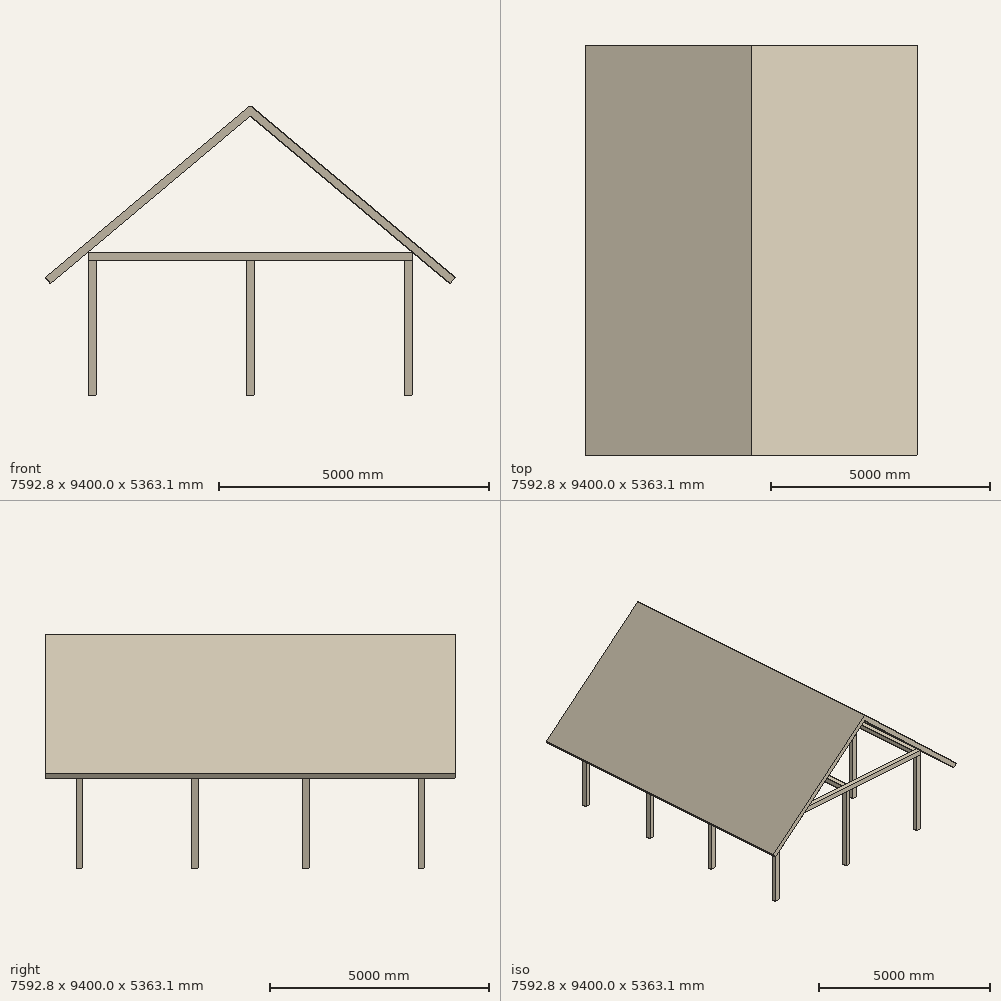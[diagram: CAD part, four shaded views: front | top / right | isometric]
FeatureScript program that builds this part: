
annotation { "Feature Type Name" : "Feature", "Feature Type Description" : "" }
export const myFeature = defineFeature(function(context is Context, id is Id, definition is map)
    precondition{}
    {
        {
            var Q0;
            Q0=qCreatedBy(makeId("Top.planeOp"),FACE);
            var sketch = newSketch(context, id + "F0", { "sketchPlane" : qUnion([Q0])});
            skLineSegment(sketch, "E0.bottom", {"start": v(-3000, 4000) * mm, "end": v(3000, 4000) * mm});
            skLineSegment(sketch, "E0.top", {"start": v(-3000, -4000) * mm, "end": v(3000, -4000) * mm});
            skLineSegment(sketch, "E0.left", {"start": v(-3000, 4000) * mm, "end": v(-3000, -4000) * mm});
            skLineSegment(sketch, "E0.right", {"start": v(3000, 4000) * mm, "end": v(3000, -4000) * mm});
            skSolve(sketch);
        }
        {
            var Q0;
            Q0=makeQuery(id+"F0.imprint","IMPRINT",FACE,{"disambiguationData":[TD([[makeQuery(id+"F0.imprint","IMPRINT",EDGE,{"derivedFrom":sQuery(id+"F0.wireOp",EDGE,"E0.bottom")}),-1.0]])]});
            extrude(context, id + "F1", {"entities" : qUnion([Q0]), "depth" : 2500 * mm});
        }
        {
            var Q0;
            Q0=makeQuery(id+"F1.opExtrude","SWEPT_FACE",FACE,{"disambiguationData":[OSD([sQuery(id+"F0.wireOp",EDGE,"E0.left")])]});
            var sketch = newSketch(context, id + "F2", { "sketchPlane" : qUnion([Q0])});
            skLineSegment(sketch, "E1.bottom", {"start": v(-3850, 0) * mm, "end": v(-1350, 0) * mm});
            skLineSegment(sketch, "E1.top", {"start": v(-3850, 2500) * mm, "end": v(-1350, 2500) * mm});
            skLineSegment(sketch, "E1.left", {"start": v(-3850, 0) * mm, "end": v(-3850, 2500) * mm});
            skLineSegment(sketch, "E1.right", {"start": v(-1350, 0) * mm, "end": v(-1350, 2500) * mm});
            skLineSegment(sketch, "E2.bottom", {"start": v(3850, 2500) * mm, "end": v(1350, 2500) * mm});
            skLineSegment(sketch, "E2.top", {"start": v(3850, 0) * mm, "end": v(1350, 0) * mm});
            skLineSegment(sketch, "E2.left", {"start": v(3850, 2500) * mm, "end": v(3850, 0) * mm});
            skLineSegment(sketch, "E2.right", {"start": v(1350, 2500) * mm, "end": v(1350, 0) * mm});
            skLineSegment(sketch, "E3.bottom", {"start": v(-1200, 2500) * mm, "end": v(1200, 2500) * mm});
            skLineSegment(sketch, "E3.top", {"start": v(-1200, 0) * mm, "end": v(1200, 0) * mm});
            skLineSegment(sketch, "E3.left", {"start": v(-1200, 2500) * mm, "end": v(-1200, 0) * mm});
            skLineSegment(sketch, "E3.right", {"start": v(1200, 2500) * mm, "end": v(1200, 0) * mm});
            skSolve(sketch);
        }
        {
            var Q0;
            Q0=makeQuery(id+"F2.imprint","IMPRINT",FACE,{"disambiguationData":[TD([[makeQuery(id+"F2.imprint","IMPRINT",EDGE,{"derivedFrom":sQuery(id+"F2.wireOp",EDGE,"E1.bottom")}),1.0]])]});
            var Q1;
            Q1=makeQuery(id+"F2.imprint","IMPRINT",FACE,{"disambiguationData":[TD([[makeQuery(id+"F2.imprint","IMPRINT",EDGE,{"derivedFrom":sQuery(id+"F2.wireOp",EDGE,"E3.bottom")}),-1.0]])]});
            var Q2;
            Q2=makeQuery(id+"F2.imprint","IMPRINT",FACE,{"disambiguationData":[TD([[makeQuery(id+"F2.imprint","IMPRINT",EDGE,{"derivedFrom":sQuery(id+"F2.wireOp",EDGE,"E2.bottom")}),-1.0]])]});
            extrude(context, id + "F3", {"entities" : qUnion([Q0, Q1, Q2]), "operationType" : NewBodyOperationType.REMOVE, "endBound" : BoundingType.THROUGH_ALL, "oppositeDirection" : true, "depth" : 25 * mm});
        }
        {
            var Q0;
            Q0=makeQuery(id+"F1.opExtrude","SWEPT_FACE",FACE,{"disambiguationData":[OSD([sQuery(id+"F0.wireOp",EDGE,"E0.top")])]});
            var sketch = newSketch(context, id + "F4", { "sketchPlane" : qUnion([Q0])});
            skLineSegment(sketch, "E4.bottom", {"start": v(-2850, 2500) * mm, "end": v(-75, 2500) * mm});
            skLineSegment(sketch, "E4.top", {"start": v(-2850, 0) * mm, "end": v(-75, 0) * mm});
            skLineSegment(sketch, "E4.left", {"start": v(-2850, 2500) * mm, "end": v(-2850, 0) * mm});
            skLineSegment(sketch, "E4.right", {"start": v(-75, 2500) * mm, "end": v(-75, 0) * mm});
            skLineSegment(sketch, "E5.bottom", {"start": v(75, 2500) * mm, "end": v(2850, 2500) * mm});
            skLineSegment(sketch, "E5.top", {"start": v(75, 0) * mm, "end": v(2850, 0) * mm});
            skLineSegment(sketch, "E5.left", {"start": v(75, 2500) * mm, "end": v(75, 0) * mm});
            skLineSegment(sketch, "E5.right", {"start": v(2850, 2500) * mm, "end": v(2850, 0) * mm});
            skSolve(sketch);
        }
        {
            var Q0;
            Q0=makeQuery(id+"F4.imprint","IMPRINT",FACE,{"disambiguationData":[TD([[makeQuery(id+"F4.imprint","IMPRINT",EDGE,{"derivedFrom":sQuery(id+"F4.wireOp",EDGE,"E4.bottom")}),-1.0]])]});
            var Q1;
            Q1=makeQuery(id+"F4.imprint","IMPRINT",FACE,{"disambiguationData":[TD([[makeQuery(id+"F4.imprint","IMPRINT",EDGE,{"derivedFrom":sQuery(id+"F4.wireOp",EDGE,"E5.bottom")}),-1.0]])]});
            extrude(context, id + "F5", {"entities" : qUnion([Q0, Q1]), "operationType" : NewBodyOperationType.REMOVE, "endBound" : BoundingType.THROUGH_ALL, "oppositeDirection" : true, "depth" : 25 * mm});
        }
        {
            var Q0;
            {var subQ0=sQuery(id+"F0.wireOp",EDGE,"E0.top");var subQ1=makeQuery(id+"F1.opExtrude","SWEPT_FACE",FACE,{"disambiguationData":[OSD([subQ0])]});var subQ2=sQuery(id+"F0.wireOp",EDGE,"E0.right");var subQ3=makeQuery(id+"F1.opExtrude","SWEPT_FACE",FACE,{"disambiguationData":[OSD([subQ2])]});var subQ5=sQuery(id+"F0.wireOp",EDGE,"E0.left");Q0=makeQuery(id+"F5.boolean.opBoolean","SPLIT",FACE,{"disambiguationData":[TD([subQ3])],"derivedFrom":makeQuery(id+"F3.boolean.opBoolean","SPLIT",FACE,{"disambiguationData":[TD([subQ1])],"derivedFrom":makeQuery(id+"F1.opExtrude","CAP_FACE",FACE,{"disambiguationData":[OSD([sQuery(id+"F0.wireOp",EDGE,"E0.bottom"),subQ0,subQ5,subQ2])],"isStart":false})})});}
            var sketch = newSketch(context, id + "F6", { "sketchPlane" : qUnion([Q0])});
            skLineSegment(sketch, "E6.bottom", {"start": v(3000, -4000) * mm, "end": v(-3000, -4000) * mm});
            skLineSegment(sketch, "E6.top", {"start": v(3000, -3850) * mm, "end": v(-3000, -3850) * mm});
            skLineSegment(sketch, "E6.left", {"start": v(3000, -4000) * mm, "end": v(3000, -3850) * mm});
            skLineSegment(sketch, "E6.right", {"start": v(-3000, -4000) * mm, "end": v(-3000, -3850) * mm});
            skLineSegment(sketch, "E7.bottom", {"start": v(3000, -1350) * mm, "end": v(-3000, -1350) * mm});
            skLineSegment(sketch, "E7.top", {"start": v(3000, -1200) * mm, "end": v(-3000, -1200) * mm});
            skLineSegment(sketch, "E7.left", {"start": v(3000, -1350) * mm, "end": v(3000, -1200) * mm});
            skLineSegment(sketch, "E7.right", {"start": v(-3000, -1350) * mm, "end": v(-3000, -1200) * mm});
            skLineSegment(sketch, "E8.bottom", {"start": v(-3000, 1200) * mm, "end": v(3000, 1200) * mm});
            skLineSegment(sketch, "E8.top", {"start": v(-3000, 1350) * mm, "end": v(3000, 1350) * mm});
            skLineSegment(sketch, "E8.left", {"start": v(-3000, 1200) * mm, "end": v(-3000, 1350) * mm});
            skLineSegment(sketch, "E8.right", {"start": v(3000, 1200) * mm, "end": v(3000, 1350) * mm});
            skLineSegment(sketch, "E9.bottom", {"start": v(3000, 3850) * mm, "end": v(-3000, 3850) * mm});
            skLineSegment(sketch, "E9.top", {"start": v(3000, 4000) * mm, "end": v(-3000, 4000) * mm});
            skLineSegment(sketch, "E9.left", {"start": v(3000, 3850) * mm, "end": v(3000, 4000) * mm});
            skLineSegment(sketch, "E9.right", {"start": v(-3000, 3850) * mm, "end": v(-3000, 4000) * mm});
            skLineSegment(sketch, "E10.bottom", {"start": v(-3000, 3850) * mm, "end": v(-2850, 3850) * mm, "construction": true});
            skLineSegment(sketch, "E10.top", {"start": v(-3000, 1350) * mm, "end": v(-2850, 1350) * mm, "construction": true});
            skLineSegment(sketch, "E10.left", {"start": v(-3000, 3850) * mm, "end": v(-3000, 1350) * mm});
            skLineSegment(sketch, "E10.right", {"start": v(-2850, 3850) * mm, "end": v(-2850, 1350) * mm});
            skLineSegment(sketch, "E11.bottom", {"start": v(-3000, 1200) * mm, "end": v(-2850, 1200) * mm, "construction": true});
            skLineSegment(sketch, "E11.top", {"start": v(-3000, -1200) * mm, "end": v(-2850, -1200) * mm, "construction": true});
            skLineSegment(sketch, "E11.left", {"start": v(-3000, 1200) * mm, "end": v(-3000, -1200) * mm});
            skLineSegment(sketch, "E11.right", {"start": v(-2850, 1200) * mm, "end": v(-2850, -1200) * mm});
            skLineSegment(sketch, "E12.bottom", {"start": v(-3000, -1350) * mm, "end": v(-2850, -1350) * mm, "construction": true});
            skLineSegment(sketch, "E12.top", {"start": v(-3000, -3850) * mm, "end": v(-2850, -3850) * mm, "construction": true});
            skLineSegment(sketch, "E12.left", {"start": v(-3000, -1350) * mm, "end": v(-3000, -3850) * mm});
            skLineSegment(sketch, "E12.right", {"start": v(-2850, -1350) * mm, "end": v(-2850, -3850) * mm});
            skLineSegment(sketch, "E13.bottom", {"start": v(3000, -1350) * mm, "end": v(2850, -1350) * mm, "construction": true});
            skLineSegment(sketch, "E13.top", {"start": v(3000, -3850) * mm, "end": v(2850, -3850) * mm, "construction": true});
            skLineSegment(sketch, "E13.left", {"start": v(3000, -1350) * mm, "end": v(3000, -3850) * mm});
            skLineSegment(sketch, "E13.right", {"start": v(2850, -1350) * mm, "end": v(2850, -3850) * mm});
            skLineSegment(sketch, "E14.bottom", {"start": v(75, -1350) * mm, "end": v(-75, -1350) * mm, "construction": true});
            skLineSegment(sketch, "E14.top", {"start": v(75, -3850) * mm, "end": v(-75, -3850) * mm, "construction": true});
            skLineSegment(sketch, "E14.left", {"start": v(75, -1350) * mm, "end": v(75, -3850) * mm});
            skLineSegment(sketch, "E14.right", {"start": v(-75, -1350) * mm, "end": v(-75, -3850) * mm});
            skLineSegment(sketch, "E15.bottom", {"start": v(75, 1200) * mm, "end": v(-75, 1200) * mm, "construction": true});
            skLineSegment(sketch, "E15.top", {"start": v(75, -1200) * mm, "end": v(-75, -1200) * mm, "construction": true});
            skLineSegment(sketch, "E15.left", {"start": v(75, 1200) * mm, "end": v(75, -1200) * mm});
            skLineSegment(sketch, "E15.right", {"start": v(-75, 1200) * mm, "end": v(-75, -1200) * mm});
            skLineSegment(sketch, "E16.bottom", {"start": v(3000, 1200) * mm, "end": v(2850, 1200) * mm, "construction": true});
            skLineSegment(sketch, "E16.top", {"start": v(3000, -1200) * mm, "end": v(2850, -1200) * mm, "construction": true});
            skLineSegment(sketch, "E16.left", {"start": v(3000, 1200) * mm, "end": v(3000, -1200) * mm});
            skLineSegment(sketch, "E16.right", {"start": v(2850, 1200) * mm, "end": v(2850, -1200) * mm});
            skLineSegment(sketch, "E17.bottom", {"start": v(3000, 3850) * mm, "end": v(2850, 3850) * mm, "construction": true});
            skLineSegment(sketch, "E17.top", {"start": v(3000, 1350) * mm, "end": v(2850, 1350) * mm, "construction": true});
            skLineSegment(sketch, "E17.left", {"start": v(3000, 3850) * mm, "end": v(3000, 1350) * mm});
            skLineSegment(sketch, "E17.right", {"start": v(2850, 3850) * mm, "end": v(2850, 1350) * mm});
            skLineSegment(sketch, "E18.bottom", {"start": v(75, 3850) * mm, "end": v(-75, 3850) * mm, "construction": true});
            skLineSegment(sketch, "E18.top", {"start": v(75, 1350) * mm, "end": v(-75, 1350) * mm, "construction": true});
            skLineSegment(sketch, "E18.left", {"start": v(75, 3850) * mm, "end": v(75, 1350) * mm});
            skLineSegment(sketch, "E18.right", {"start": v(-75, 3850) * mm, "end": v(-75, 1350) * mm});
            skSolve(sketch);
        }
        {
            var Q0;
            {var subQ8=sQuery(id+"F6.wireOp",EDGE,"E6.right");Q0=makeQuery(id+"F6.imprint","IMPRINT",FACE,{"disambiguationData":[TD([[makeQuery(id+"F6.imprint","IMPRINT",EDGE,{"derivedFrom":subQ8}),-1.0]])]});}
            var Q1;
            {var subQ6=sQuery(id+"F6.wireOp",EDGE,"E7.left");Q1=makeQuery(id+"F6.imprint","IMPRINT",FACE,{"disambiguationData":[TD([[makeQuery(id+"F6.imprint","IMPRINT",EDGE,{"derivedFrom":subQ6}),1.0]])]});}
            var Q2;
            Q2=makeQuery(id+"F6.imprint","IMPRINT",FACE,{"disambiguationData":[TD([[makeQuery(id+"F6.imprint","IMPRINT",EDGE,{"derivedFrom":sQuery(id+"F6.wireOp",EDGE,"E9.top")}),1.0]])]});
            var Q3;
            {var subQ6=sQuery(id+"F6.wireOp",EDGE,"E8.left");Q3=makeQuery(id+"F6.imprint","IMPRINT",FACE,{"disambiguationData":[TD([[makeQuery(id+"F6.imprint","IMPRINT",EDGE,{"derivedFrom":subQ6}),-1.0]])]});}
            var Q4;
            {var subQ0=sQuery(id+"F6.wireOp",EDGE,"E6.left");Q4=makeQuery(id+"F6.imprint","IMPRINT",FACE,{"disambiguationData":[TD([[makeQuery(id+"F6.imprint","IMPRINT",EDGE,{"derivedFrom":subQ0}),-1.0]])]});}
            extrude(context, id + "F7", {"entities" : qUnion([Q0, Q1, Q2, Q3, Q4]), "depth" : 150 * mm});
        }
        {
            var Q0;
            Q0=makeQuery(id+"F7.opExtrude","CAP_FACE",FACE,{"disambiguationData":[OSD([sQuery(id+"F0.wireOp",EDGE,"E0.top"),sQuery(id+"F4.wireOp",EDGE,"E5.bottom"),sQuery(id+"F4.wireOp",EDGE,"E5.right"),sQuery(id+"F6.wireOp",EDGE,"E6.bottom"),sQuery(id+"F6.wireOp",EDGE,"E6.top"),sQuery(id+"F6.wireOp",EDGE,"E6.right")])],"isStart":false});
            var sketch = newSketch(context, id + "F8", { "sketchPlane" : qUnion([Q0])});
            skLineSegment(sketch, "E19.bottom", {"start": v(-3000, 3850) * mm, "end": v(-2850, 3850) * mm});
            skLineSegment(sketch, "E19.top", {"start": v(-3000, 1350) * mm, "end": v(-2850, 1350) * mm});
            skLineSegment(sketch, "E19.left", {"start": v(-3000, 3850) * mm, "end": v(-3000, 1350) * mm});
            skLineSegment(sketch, "E19.right", {"start": v(-2850, 3850) * mm, "end": v(-2850, 1350) * mm});
            skLineSegment(sketch, "E20.bottom", {"start": v(-3000, 1200) * mm, "end": v(-2850, 1200) * mm});
            skLineSegment(sketch, "E20.top", {"start": v(-3000, -1200) * mm, "end": v(-2850, -1200) * mm});
            skLineSegment(sketch, "E20.left", {"start": v(-3000, 1200) * mm, "end": v(-3000, -1200) * mm});
            skLineSegment(sketch, "E20.right", {"start": v(-2850, 1200) * mm, "end": v(-2850, -1200) * mm});
            skLineSegment(sketch, "E21.bottom", {"start": v(-3000, -1350) * mm, "end": v(-2850, -1350) * mm});
            skLineSegment(sketch, "E21.top", {"start": v(-3000, -3850) * mm, "end": v(-2850, -3850) * mm});
            skLineSegment(sketch, "E21.left", {"start": v(-3000, -1350) * mm, "end": v(-3000, -3850) * mm});
            skLineSegment(sketch, "E21.right", {"start": v(-2850, -1350) * mm, "end": v(-2850, -3850) * mm});
            skLineSegment(sketch, "E22.bottom", {"start": v(3000, -3850) * mm, "end": v(2850, -3850) * mm});
            skLineSegment(sketch, "E22.top", {"start": v(3000, -1350) * mm, "end": v(2850, -1350) * mm});
            skLineSegment(sketch, "E22.left", {"start": v(3000, -3850) * mm, "end": v(3000, -1350) * mm});
            skLineSegment(sketch, "E22.right", {"start": v(2850, -3850) * mm, "end": v(2850, -1350) * mm});
            skLineSegment(sketch, "E23.bottom", {"start": v(2850, -1200) * mm, "end": v(3000, -1200) * mm});
            skLineSegment(sketch, "E23.top", {"start": v(2850, 1200) * mm, "end": v(3000, 1200) * mm});
            skLineSegment(sketch, "E23.left", {"start": v(2850, -1200) * mm, "end": v(2850, 1200) * mm});
            skLineSegment(sketch, "E23.right", {"start": v(3000, -1200) * mm, "end": v(3000, 1200) * mm});
            skLineSegment(sketch, "E24.bottom", {"start": v(2850, 1350) * mm, "end": v(3000, 1350) * mm});
            skLineSegment(sketch, "E24.top", {"start": v(2850, 3850) * mm, "end": v(3000, 3850) * mm});
            skLineSegment(sketch, "E24.left", {"start": v(2850, 1350) * mm, "end": v(2850, 3850) * mm});
            skLineSegment(sketch, "E24.right", {"start": v(3000, 1350) * mm, "end": v(3000, 3850) * mm});
            skLineSegment(sketch, "E25.bottom", {"start": v(-75, 3850) * mm, "end": v(75, 3850) * mm});
            skLineSegment(sketch, "E25.top", {"start": v(-75, 1350) * mm, "end": v(75, 1350) * mm});
            skLineSegment(sketch, "E25.left", {"start": v(-75, 3850) * mm, "end": v(-75, 1350) * mm});
            skLineSegment(sketch, "E25.right", {"start": v(75, 3850) * mm, "end": v(75, 1350) * mm});
            skLineSegment(sketch, "E26.bottom", {"start": v(-75, 1200) * mm, "end": v(75, 1200) * mm});
            skLineSegment(sketch, "E26.top", {"start": v(-75, -1200) * mm, "end": v(75, -1200) * mm});
            skLineSegment(sketch, "E26.left", {"start": v(-75, 1200) * mm, "end": v(-75, -1200) * mm});
            skLineSegment(sketch, "E26.right", {"start": v(75, 1200) * mm, "end": v(75, -1200) * mm});
            skLineSegment(sketch, "E27.bottom", {"start": v(-75, -1350) * mm, "end": v(75, -1350) * mm});
            skLineSegment(sketch, "E27.top", {"start": v(-75, -3850) * mm, "end": v(75, -3850) * mm});
            skLineSegment(sketch, "E27.left", {"start": v(-75, -1350) * mm, "end": v(-75, -3850) * mm});
            skLineSegment(sketch, "E27.right", {"start": v(75, -1350) * mm, "end": v(75, -3850) * mm});
            skLineSegment(sketch, "E28.0", {"start": v(75, 4000) * mm, "end": v(75, 3850) * mm});
            skLineSegment(sketch, "E29.0", {"start": v(-75, 4000) * mm, "end": v(-75, 3850) * mm});
            skSolve(sketch);
        }
        {
            var Q0;
            Q0=makeQuery(id+"F8.imprint","IMPRINT",FACE,{"disambiguationData":[TD([[makeQuery(id+"F8.imprint","IMPRINT",EDGE,{"derivedFrom":sQuery(id+"F8.wireOp",EDGE,"E21.bottom")}),-1.0]])]});
            var Q1;
            Q1=makeQuery(id+"F8.imprint","IMPRINT",FACE,{"disambiguationData":[TD([[makeQuery(id+"F8.imprint","IMPRINT",EDGE,{"derivedFrom":sQuery(id+"F8.wireOp",EDGE,"E22.bottom")}),-1.0]])]});
            var Q2;
            Q2=makeQuery(id+"F8.imprint","IMPRINT",FACE,{"disambiguationData":[TD([[makeQuery(id+"F8.imprint","IMPRINT",EDGE,{"derivedFrom":sQuery(id+"F8.wireOp",EDGE,"E23.bottom")}),1.0]])]});
            var Q3;
            Q3=makeQuery(id+"F8.imprint","IMPRINT",FACE,{"disambiguationData":[TD([[makeQuery(id+"F8.imprint","IMPRINT",EDGE,{"derivedFrom":sQuery(id+"F8.wireOp",EDGE,"E20.bottom")}),-1.0]])]});
            var Q4;
            Q4=makeQuery(id+"F8.imprint","IMPRINT",FACE,{"disambiguationData":[TD([[makeQuery(id+"F8.imprint","IMPRINT",EDGE,{"derivedFrom":sQuery(id+"F8.wireOp",EDGE,"E19.bottom")}),-1.0]])]});
            var Q5;
            Q5=makeQuery(id+"F8.imprint","IMPRINT",FACE,{"disambiguationData":[TD([[makeQuery(id+"F8.imprint","IMPRINT",EDGE,{"derivedFrom":sQuery(id+"F8.wireOp",EDGE,"E24.bottom")}),1.0]])]});
            var Q6;
            Q6=makeQuery(id+"F8.imprint","IMPRINT",FACE,{"disambiguationData":[TD([[makeQuery(id+"F8.imprint","IMPRINT",EDGE,{"derivedFrom":sQuery(id+"F8.wireOp",EDGE,"E25.bottom")}),-1.0]])]});
            var Q7;
            Q7=makeQuery(id+"F8.imprint","IMPRINT",FACE,{"disambiguationData":[TD([[makeQuery(id+"F8.imprint","IMPRINT",EDGE,{"derivedFrom":sQuery(id+"F8.wireOp",EDGE,"E26.bottom")}),-1.0]])]});
            var Q8;
            Q8=makeQuery(id+"F8.imprint","IMPRINT",FACE,{"disambiguationData":[TD([[makeQuery(id+"F8.imprint","IMPRINT",EDGE,{"derivedFrom":sQuery(id+"F8.wireOp",EDGE,"E27.bottom")}),-1.0]])]});
            extrude(context, id + "F9", {"entities" : qUnion([Q0, Q1, Q2, Q3, Q4, Q5, Q6, Q7, Q8]), "oppositeDirection" : true, "depth" : 150 * mm});
        }
        {
            var Q0;
            Q0=makeQuery(id+"F7.opExtrude","SWEPT_FACE",FACE,{"disambiguationData":[OSD([sQuery(id+"F6.wireOp",EDGE,"E6.bottom")])]});
            var sketch = newSketch(context, id + "F10", { "sketchPlane" : qUnion([Q0])});
            skLineSegment(sketch, "E30", {"start": v(-3796.42, 2177.54) * mm, "end": v(0, 5363.1) * mm});
            skLineSegment(sketch, "E31", {"start": v(0, 5363.1) * mm, "end": v(3796.42, 2177.54) * mm});
            skLineSegment(sketch, "E32", {"start": v(0, 5167.3) * mm, "end": v(-3700, 2062.63) * mm});
            skLineSegment(sketch, "E33", {"start": v(-3700, 2062.63) * mm, "end": v(-3796.42, 2177.54) * mm});
            skLineSegment(sketch, "E34", {"start": v(3796.42, 2177.54) * mm, "end": v(3700, 2062.63) * mm});
            skLineSegment(sketch, "E35", {"start": v(3700, 2062.63) * mm, "end": v(0, 5167.3) * mm});
            skSolve(sketch);
        }
        {
            var Q0;
            Q0=makeQuery(id+"F10.imprint","IMPRINT",FACE,{"disambiguationData":[TD([[makeQuery(id+"F10.imprint","IMPRINT",EDGE,{"derivedFrom":sQuery(id+"F10.wireOp",EDGE,"E30")}),-1.0]])]});
            extrude(context, id + "F11", {"entities" : qUnion([Q0]), "depth" : 700 * mm, "hasSecondDirection" : true, "secondDirectionOppositeDirection" : true, "secondDirectionDepth" : 8700 * mm});
        }
    });
